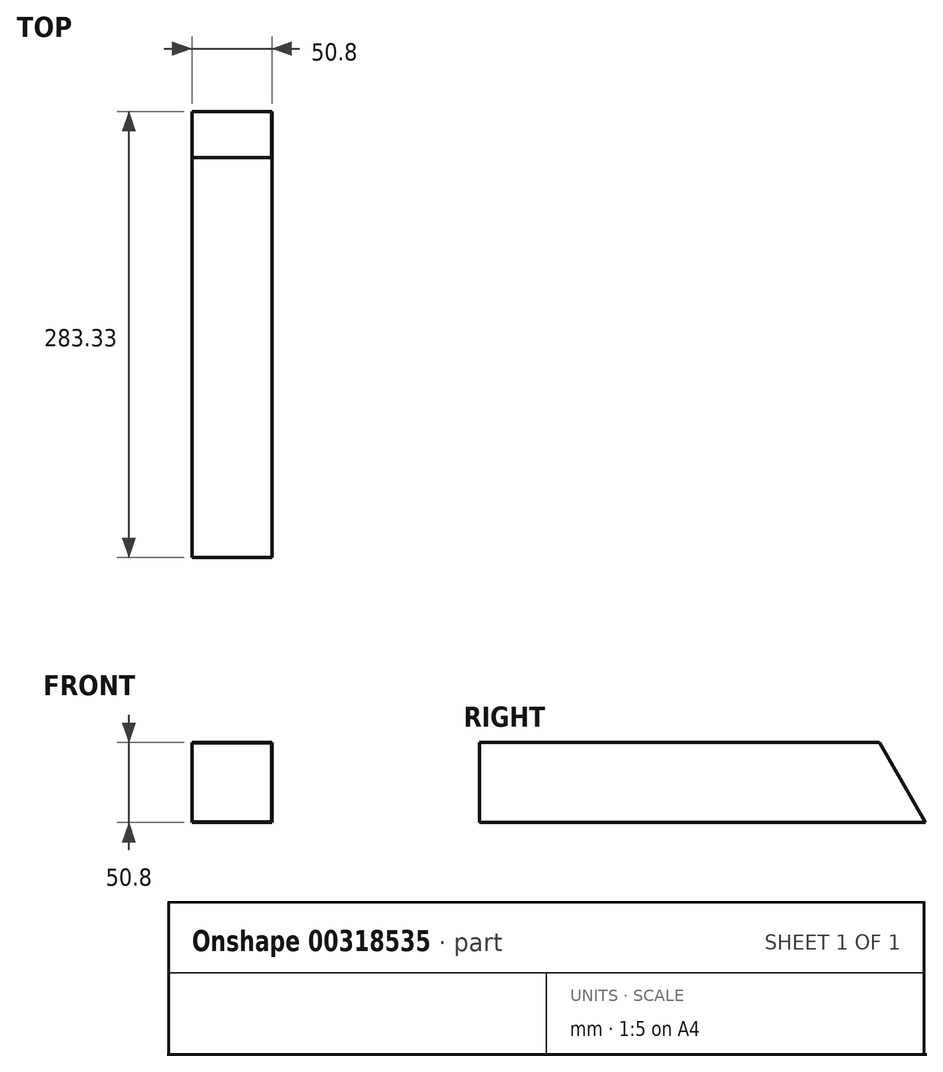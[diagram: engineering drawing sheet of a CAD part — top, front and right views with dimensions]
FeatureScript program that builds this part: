
annotation { "Feature Type Name" : "Feature", "Feature Type Description" : "" }
export const myFeature = defineFeature(function(context is Context, id is Id, definition is map)
    precondition{}
    {
        {
            var Q0;
            Q0=qCreatedBy(makeId("Right.planeOp"),FACE);
            var sketch = newSketch(context, id + "F0", { "sketchPlane" : qUnion([Q0])});
            skLineSegment(sketch, "E0", {"start": v(-172.62, 60.17) * mm, "end": v(81.38, 60.17) * mm});
            skLineSegment(sketch, "E1", {"start": v(81.38, 60.17) * mm, "end": v(110.7, 9.37) * mm});
            skLineSegment(sketch, "E2", {"start": v(110.7, 9.37) * mm, "end": v(-172.62, 9.37) * mm});
            skLineSegment(sketch, "E3", {"start": v(-172.62, 9.37) * mm, "end": v(-172.62, 60.17) * mm});
            skSolve(sketch);
        }
        {
            var Q0;
            Q0=makeQuery(id+"F0.imprint","IMPRINT",FACE,{"disambiguationData":[TD([[makeQuery(id+"F0.imprint","IMPRINT",EDGE,{"derivedFrom":sQuery(id+"F0.wireOp",EDGE,"E0")}),-1.0]])]});
            extrude(context, id + "F1", {"entities" : qUnion([Q0]), "endBound" : BoundingType.SYMMETRIC, "depth" : 50.8 * mm});
        }
        {
            var Q0;
            Q0=makeQuery(id+"F1.opExtrude","SWEPT_FACE",FACE,{"disambiguationData":[OSD([sQuery(id+"F0.wireOp",EDGE,"E3")])]});
            var sketch = newSketch(context, id + "F2", { "sketchPlane" : qUnion([Q0])});
            skLineSegment(sketch, "E4.bottom", {"start": v(25.1, 9.68) * mm, "end": v(-25.1, 9.68) * mm});
            skLineSegment(sketch, "E4.top", {"start": v(25.1, 59.87) * mm, "end": v(-25.1, 59.87) * mm});
            skLineSegment(sketch, "E4.left", {"start": v(25.1, 9.68) * mm, "end": v(25.1, 59.87) * mm});
            skLineSegment(sketch, "E4.right", {"start": v(-25.1, 9.68) * mm, "end": v(-25.1, 59.87) * mm});
            skPoint(sketch, "E4.middle", {"position": v(0, 34.77) * mm});
            skPoint(sketch, "E4.middle.positionSnap0", {"position": v(-25.4, 34.77) * mm});
            skPoint(sketch, "E4.centerSnap0", {"position": v(-25.4, 34.77) * mm});
            skSolve(sketch);
        }
        {
            var Q0;
            Q0=makeQuery(id+"F2.imprint","IMPRINT",FACE,{"disambiguationData":[TD([[makeQuery(id+"F2.imprint","IMPRINT",EDGE,{"derivedFrom":sQuery(id+"F2.wireOp",EDGE,"E4.bottom")}),-1.0]])]});
            extrude(context, id + "F3", {"entities" : qUnion([Q0]), "operationType" : NewBodyOperationType.REMOVE, "endBound" : BoundingType.THROUGH_ALL, "oppositeDirection" : true, "depth" : 25.4 * mm});
        }
    });
